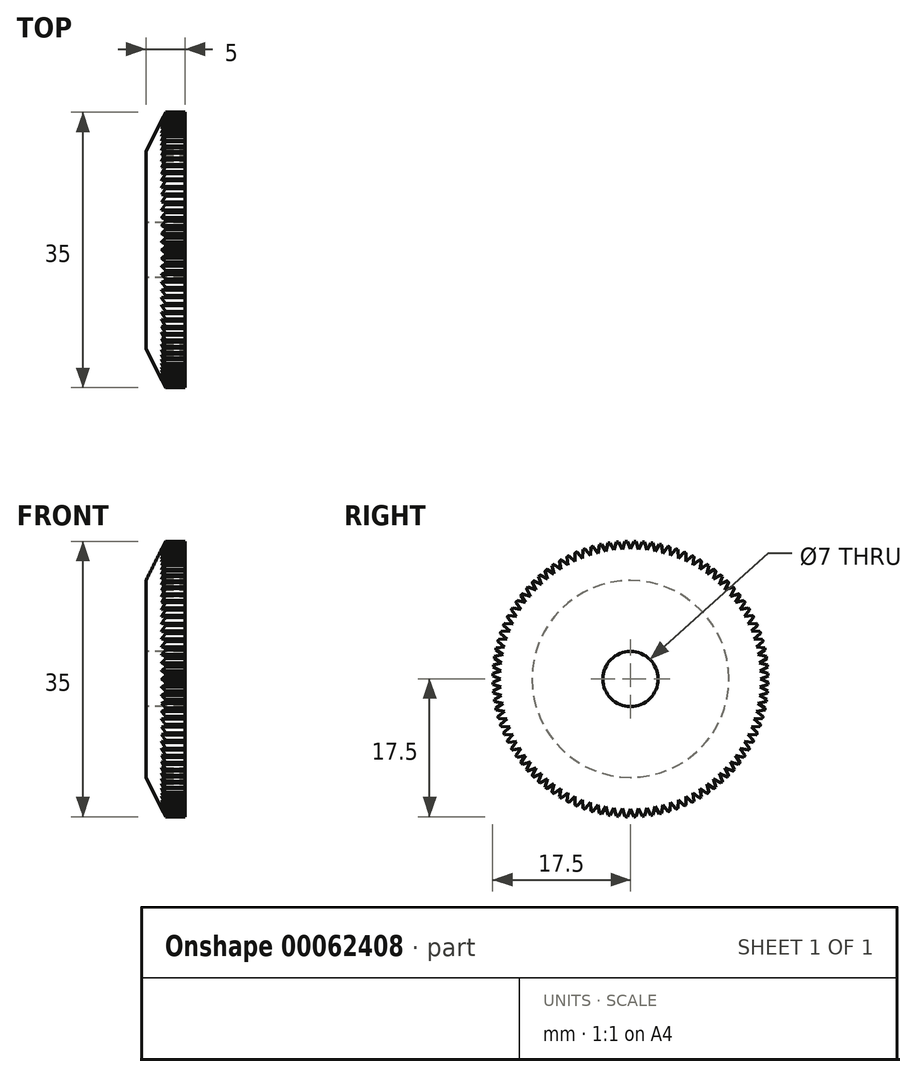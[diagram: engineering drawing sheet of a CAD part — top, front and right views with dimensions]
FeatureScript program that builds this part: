
annotation { "Feature Type Name" : "Feature", "Feature Type Description" : "" }
export const myFeature = defineFeature(function(context is Context, id is Id, definition is map)
    precondition{}
    {
        {
            var Q0;
            Q0=qCreatedBy(makeId("Front.planeOp"),FACE);
            var sketch = newSketch(context, id + "F0", { "sketchPlane" : qUnion([Q0])});
            skLineSegment(sketch, "E0", {"start": v(0, 3.5) * mm, "end": v(0, 12.5) * mm});
            skLineSegment(sketch, "E1", {"start": v(0, 12.5) * mm, "end": v(2.5, 17.5) * mm});
            skLineSegment(sketch, "E2", {"start": v(2.5, 17.5) * mm, "end": v(5, 17.5) * mm});
            skLineSegment(sketch, "E3", {"start": v(5, 17.5) * mm, "end": v(5, 3.5) * mm});
            skLineSegment(sketch, "E4", {"start": v(5, 3.5) * mm, "end": v(0, 3.5) * mm});
            skLineSegment(sketch, "E5", {"start": v(0, 0) * mm, "end": v(8.1, 0) * mm, "construction": true});
            skSolve(sketch);
        }
        {
            var Q0;
            Q0 = qSketchRegion(id + "F0", true);
            var Q1;
            Q1=sQuery(id+"F0.wireOp",EDGE,"E5");
            revolve(context, id + "F1", {"entities" : qUnion([Q0]), "axis" : qUnion([Q1]), "revolveType" : RevolveType.FULL});
        }
        {
            var Q0;
            Q0=makeQuery(id+"F1.opRevolve","SWEPT_FACE",FACE,{"disambiguationData":[OSD([sQuery(id+"F0.wireOp",EDGE,"E3")])]});
            var sketch = newSketch(context, id + "F2", { "sketchPlane" : qUnion([Q0])});
            skLineSegment(sketch, "E6", {"start": v(-0.41, 17.5) * mm, "end": v(0, 16.5) * mm});
            skLineSegment(sketch, "E7", {"start": v(0, 16.5) * mm, "end": v(0.41, 17.5) * mm});
            skLineSegment(sketch, "E8", {"start": v(0, 0) * mm, "end": v(0, 16.5) * mm, "construction": true});
            skArc(sketch, "E9.0", {"start": v(0.41, 17.5) * mm, "mid": v(0, 17.5) * mm, "end": v(-0.41, 17.5) * mm});
            skSolve(sketch);
        }
        {
            var Q0;
            Q0 = qSketchRegion(id + "F2", true);
            extrude(context, id + "F3", {"entities" : qUnion([Q0]), "operationType" : NewBodyOperationType.REMOVE, "endBound" : BoundingType.UP_TO_NEXT, "oppositeDirection" : true, "depth" : 25 * mm});
        }
        {
            var Q0;
            Q0=makeQuery(id+"F3.boolean.opBoolean","COPY",FACE,{"derivedFrom":makeQuery(id+"F3.opExtrude","SWEPT_FACE",FACE,{"disambiguationData":[OSD([sQuery(id+"F2.wireOp",EDGE,"E6")])]})});
            var Q1;
            Q1=makeQuery(id+"F3.boolean.opBoolean","COPY",FACE,{"derivedFrom":makeQuery(id+"F3.opExtrude","SWEPT_FACE",FACE,{"disambiguationData":[OSD([sQuery(id+"F2.wireOp",EDGE,"E7")])]})});
            var Q2;
            Q2=makeQuery(id+"F1.opRevolve","SWEPT_FACE",FACE,{"disambiguationData":[OSD([sQuery(id+"F0.wireOp",EDGE,"E4")])]});
            circularPattern(context, id + "F4", {"operationType" : NewBodyOperationType.REMOVE, "faces" : qUnion([Q0, Q1]), "axis" : qUnion([Q2]), "angle" : 360 * degree, "instanceCount" : 100, "oppositeDirection" : true, "equalSpace" : true, "patternType" : PatternType.FACE});
        }
    });
